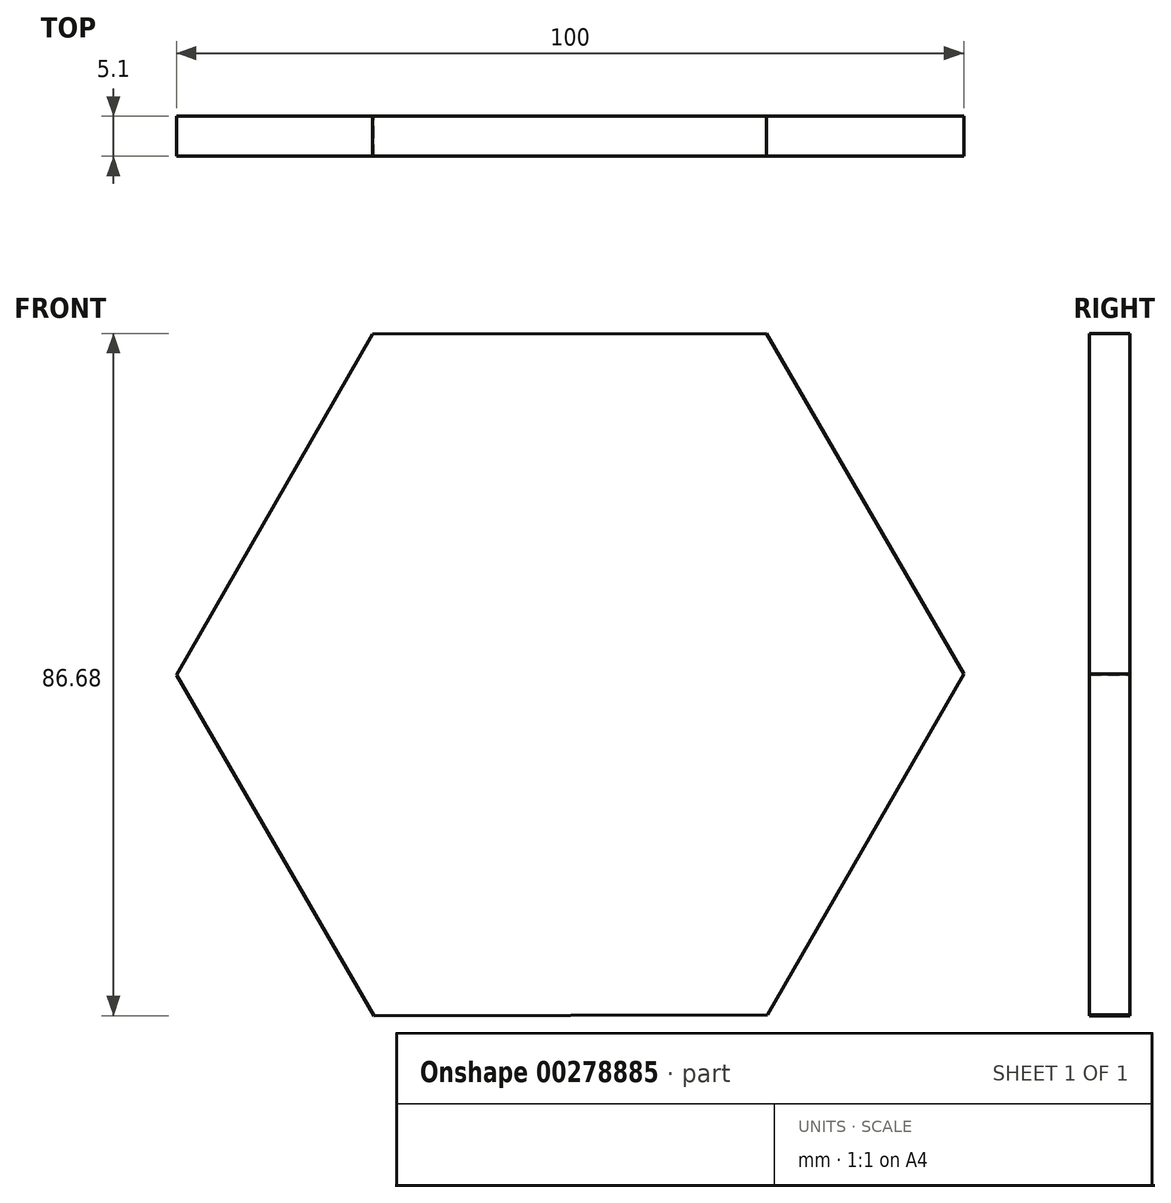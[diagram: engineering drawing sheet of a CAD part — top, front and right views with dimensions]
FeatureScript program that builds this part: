
annotation { "Feature Type Name" : "Feature", "Feature Type Description" : "" }
export const myFeature = defineFeature(function(context is Context, id is Id, definition is map)
    precondition{}
    {
        {
            var Q0;
            Q0=qCreatedBy(makeId("Front.planeOp"),FACE);
            var sketch = newSketch(context, id + "F0", { "sketchPlane" : qUnion([Q0])});
            skCircle(sketch, "E0.cCircle", {"center": v(0, 0) * mm, "radius": 43.3 * mm, "construction": true});
            skLineSegment(sketch, "E0.0", {"start": v(-50, -0.08) * mm, "end": v(-25.07, 43.26) * mm});
            skLineSegment(sketch, "E0.1", {"start": v(-25.07, 43.26) * mm, "end": v(24.93, 43.34) * mm});
            skLineSegment(sketch, "E0.2", {"start": v(24.93, 43.34) * mm, "end": v(50, 0.08) * mm});
            skLineSegment(sketch, "E0.3", {"start": v(50, 0.08) * mm, "end": v(25.07, -43.26) * mm});
            skLineSegment(sketch, "E0.4", {"start": v(25.07, -43.26) * mm, "end": v(-24.93, -43.34) * mm});
            skLineSegment(sketch, "E0.5", {"start": v(-24.93, -43.34) * mm, "end": v(-50, -0.08) * mm});
            skPoint(sketch, "E0.0.midPoint", {"position": v(-37.54, 21.59) * mm});
            skSolve(sketch);
        }
        {
            var Q0;
            Q0=makeQuery(id+"F0.imprint","IMPRINT",FACE,{"disambiguationData":[TD([[makeQuery(id+"F0.imprint","IMPRINT",EDGE,{"derivedFrom":sQuery(id+"F0.wireOp",EDGE,"E0.0")}),-1.0]])]});
            extrude(context, id + "F1", {"entities" : qUnion([Q0]), "depth" : 5.1 * mm});
        }
    });
